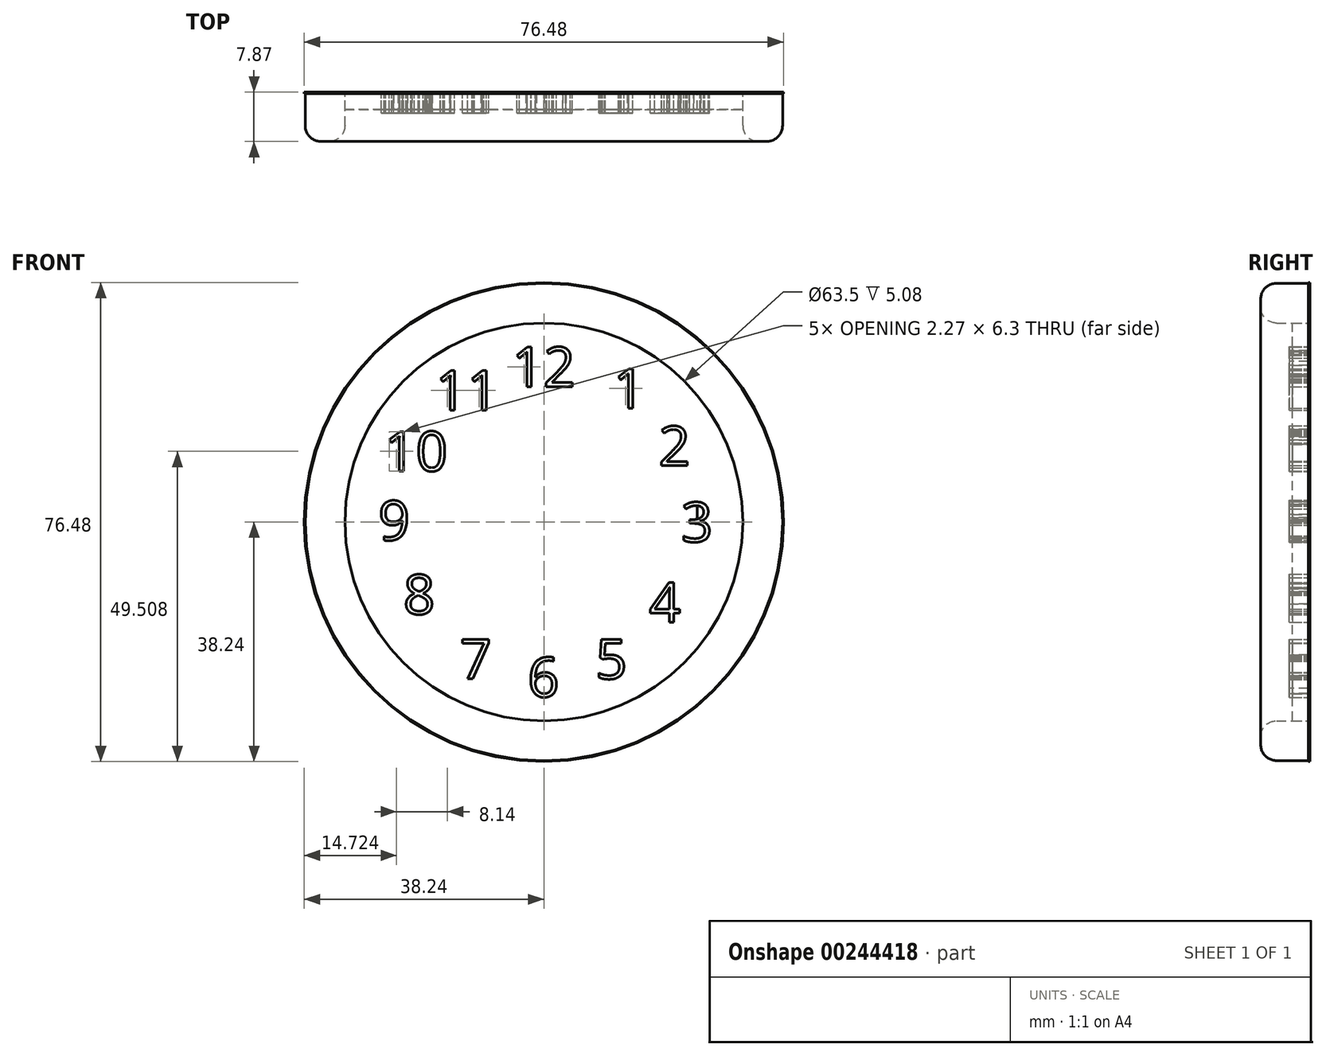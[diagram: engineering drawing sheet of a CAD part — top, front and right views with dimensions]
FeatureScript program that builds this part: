
annotation { "Feature Type Name" : "Feature", "Feature Type Description" : "" }
export const myFeature = defineFeature(function(context is Context, id is Id, definition is map)
    precondition{}
    {
        {
            var Q0;
            Q0=qCreatedBy(makeId("Front.planeOp"),FACE);
            var sketch = newSketch(context, id + "F0", { "sketchPlane" : qUnion([Q0])});
            skCircle(sketch, "E0", {"center": v(0, 0) * mm, "radius": 38.1 * mm});
            skCircle(sketch, "E1", {"center": v(0, 0) * mm, "radius": 31.75 * mm});
            skCircle(sketch, "E2", {"center": v(0, 0) * mm, "radius": 1.27 * mm, "construction": true});
            skText(sketch, "E3", { "text": "12", "fontName": "OpenSans-Regular.ttf"});
            skText(sketch, "E4", { "text": "1\n", "fontName": "OpenSans-Regular.ttf"});
            skText(sketch, "E5", { "text": "2", "fontName": "OpenSans-Regular.ttf"});
            skText(sketch, "E6", { "text": "10", "fontName": "OpenSans-Regular.ttf"});
            skText(sketch, "E7", { "text": "11", "fontName": "OpenSans-Regular.ttf"});
            skText(sketch, "E8", { "text": "4", "fontName": "OpenSans-Regular.ttf"});
            skText(sketch, "E9", { "text": "3", "fontName": "OpenSans-Regular.ttf"});
            skLineSegment(sketch, "E10", {"start": v(24.46, 0) * mm, "end": v(24.46, 3.18) * mm});
            skLineSegment(sketch, "E11", {"start": v(-23.86, 0) * mm, "end": v(-23.86, 3.42) * mm, "construction": true});
            skText(sketch, "E12", { "text": "5", "fontName": "OpenSans-Regular.ttf"});
            skText(sketch, "E13", { "text": "6", "fontName": "OpenSans-Regular.ttf"});
            skText(sketch, "E14", { "text": "9", "fontName": "OpenSans-Regular.ttf"});
            skText(sketch, "E15", { "text": "7", "fontName": "OpenSans-Regular.ttf"});
            skText(sketch, "E16", { "text": "8", "fontName": "OpenSans-Regular.ttf"});
            const initialGuessF0  = {"E3": [-0.0051, 0.0216, 1, 0, 0.00635], "E4": [0.0111, 0.01815, 1, 0, 0.00635], "E5": [0.01832, 0.00897, 1, 0, 0.00635], "E6": [-0.02546, 0.00812, 1, 0, 0.00635], "E7": [-0.01732, 0.01785, 1, 0, 0.00635], "E8": [0.0168, -0.016, 1, 0, 0.00635], "E9": [0.0219, -0.00318, 1, 0, 0.00635], "E12": [0.00824, -0.02505, 1, 0, 0.00635], "E13": [-0.0026, -0.02794, 1, 0, 0.00635], "E14": [-0.02643, -0.00293, 1, 0, 0.00635], "E15": [-0.01338, -0.02505, 1, 0, 0.00635], "E16": [-0.02243, -0.01473, 1, 0, 0.00635]};
            skSetInitialGuess(sketch, initialGuessF0);
            skSolve(sketch);
        }
        {
            var Q0;
            Q0=makeQuery(id+"F0.imprint","IMPRINT",FACE,{"disambiguationData":[TD([[makeQuery(id+"F0.imprint","IMPRINT",EDGE,{"derivedFrom":sQuery(id+"F0.wireOp",EDGE,"E0")}),1.0]])]});
            extrude(context, id + "F1", {"entities" : qUnion([Q0]), "depth" : 7.62 * mm});
        }
        {
            var Q0;
            Q0=makeQuery(id+"F0.imprint","IMPRINT",FACE,{"disambiguationData":[TD([[makeQuery(id+"F0.imprint","IMPRINT",EDGE,{"derivedFrom":sQuery(id+"F0.wireOp",EDGE,"E6.sketch_text.stroke-17")}),1.0]])]});
            extrude(context, id + "F2", {"entities" : qUnion([Q0]), "depth" : 2.54 * mm});
        }
        {
            var Q0;
            Q0=makeQuery(id+"F0.imprint","IMPRINT",FACE,{"disambiguationData":[TD([[makeQuery(id+"F0.imprint","IMPRINT",EDGE,{"derivedFrom":sQuery(id+"F0.wireOp",EDGE,"E8.sketch_text.stroke-11")}),1.0]])]});
            extrude(context, id + "F3", {"entities" : qUnion([Q0]), "depth" : 2.54 * mm});
        }
        {
            var Q0;
            Q0=makeQuery(id+"F0.imprint","IMPRINT",FACE,{"disambiguationData":[TD([[makeQuery(id+"F0.imprint","IMPRINT",EDGE,{"derivedFrom":sQuery(id+"F0.wireOp",EDGE,"E14.sketch_text.stroke-16")}),1.0]])]});
            extrude(context, id + "F4", {"entities" : qUnion([Q0]), "depth" : 2.54 * mm});
        }
        {
            var Q0;
            Q0=makeQuery(id+"F0.imprint","IMPRINT",FACE,{"disambiguationData":[TD([[makeQuery(id+"F0.imprint","IMPRINT",EDGE,{"derivedFrom":sQuery(id+"F0.wireOp",EDGE,"E13.sketch_text.stroke-15")}),1.0]])]});
            var Q1;
            Q1=makeQuery(id+"F0.imprint","IMPRINT",FACE,{"disambiguationData":[TD([[makeQuery(id+"F0.imprint","IMPRINT",EDGE,{"derivedFrom":sQuery(id+"F0.wireOp",EDGE,"E16.sketch_text.stroke-15")}),1.0]])]});
            var Q2;
            Q2=makeQuery(id+"F0.imprint","IMPRINT",FACE,{"disambiguationData":[TD([[makeQuery(id+"F0.imprint","IMPRINT",EDGE,{"derivedFrom":sQuery(id+"F0.wireOp",EDGE,"E16.sketch_text.stroke-23")}),1.0]])]});
            extrude(context, id + "F5", {"entities" : qUnion([Q0, Q1, Q2]), "depth" : 2.54 * mm});
        }
        {
            var Q0;
            Q0=makeQuery(id+"F0.imprint","IMPRINT",FACE,{"disambiguationData":[TD([[makeQuery(id+"F0.imprint","IMPRINT",EDGE,{"derivedFrom":sQuery(id+"F0.wireOp",EDGE,"E9.sketch_text.stroke-0")}),-1.0]])]});
            var Q1;
            Q1=makeQuery(id+"F0.imprint","IMPRINT",FACE,{"disambiguationData":[TD([[makeQuery(id+"F0.imprint","IMPRINT",EDGE,{"derivedFrom":sQuery(id+"F0.wireOp",EDGE,"E8.sketch_text.stroke-0")}),-1.0]])]});
            var Q2;
            Q2=makeQuery(id+"F0.imprint","IMPRINT",FACE,{"disambiguationData":[TD([[makeQuery(id+"F0.imprint","IMPRINT",EDGE,{"derivedFrom":sQuery(id+"F0.wireOp",EDGE,"E12.sketch_text.stroke-0")}),-1.0]])]});
            var Q3;
            Q3=makeQuery(id+"F0.imprint","IMPRINT",FACE,{"disambiguationData":[TD([[makeQuery(id+"F0.imprint","IMPRINT",EDGE,{"derivedFrom":sQuery(id+"F0.wireOp",EDGE,"E13.sketch_text.stroke-0")}),-1.0]])]});
            var Q4;
            Q4=makeQuery(id+"F0.imprint","IMPRINT",FACE,{"disambiguationData":[TD([[makeQuery(id+"F0.imprint","IMPRINT",EDGE,{"derivedFrom":sQuery(id+"F0.wireOp",EDGE,"E15.sketch_text.stroke-0")}),-1.0]])]});
            var Q5;
            Q5=makeQuery(id+"F0.imprint","IMPRINT",FACE,{"disambiguationData":[TD([[makeQuery(id+"F0.imprint","IMPRINT",EDGE,{"derivedFrom":sQuery(id+"F0.wireOp",EDGE,"E16.sketch_text.stroke-0")}),-1.0]])]});
            var Q6;
            Q6=makeQuery(id+"F0.imprint","IMPRINT",FACE,{"disambiguationData":[TD([[makeQuery(id+"F0.imprint","IMPRINT",EDGE,{"derivedFrom":sQuery(id+"F0.wireOp",EDGE,"E14.sketch_text.stroke-0")}),-1.0]])]});
            var Q7;
            Q7=makeQuery(id+"F0.imprint","IMPRINT",FACE,{"disambiguationData":[TD([[makeQuery(id+"F0.imprint","IMPRINT",EDGE,{"derivedFrom":sQuery(id+"F0.wireOp",EDGE,"E6.sketch_text.stroke-9")}),-1.0]])]});
            var Q8;
            Q8=makeQuery(id+"F0.imprint","IMPRINT",FACE,{"disambiguationData":[TD([[makeQuery(id+"F0.imprint","IMPRINT",EDGE,{"derivedFrom":sQuery(id+"F0.wireOp",EDGE,"E6.sketch_text.stroke-0")}),-1.0]])]});
            var Q9;
            Q9=makeQuery(id+"F0.imprint","IMPRINT",FACE,{"disambiguationData":[TD([[makeQuery(id+"F0.imprint","IMPRINT",EDGE,{"derivedFrom":sQuery(id+"F0.wireOp",EDGE,"E5.sketch_text.stroke-0")}),-1.0]])]});
            var Q10;
            Q10=makeQuery(id+"F0.imprint","IMPRINT",FACE,{"disambiguationData":[TD([[makeQuery(id+"F0.imprint","IMPRINT",EDGE,{"derivedFrom":sQuery(id+"F0.wireOp",EDGE,"E4.sketch_text.stroke-0")}),-1.0]])]});
            var Q11;
            Q11=makeQuery(id+"F0.imprint","IMPRINT",FACE,{"disambiguationData":[TD([[makeQuery(id+"F0.imprint","IMPRINT",EDGE,{"derivedFrom":sQuery(id+"F0.wireOp",EDGE,"E3.sketch_text.stroke-9")}),-1.0]])]});
            var Q12;
            Q12=makeQuery(id+"F0.imprint","IMPRINT",FACE,{"disambiguationData":[TD([[makeQuery(id+"F0.imprint","IMPRINT",EDGE,{"derivedFrom":sQuery(id+"F0.wireOp",EDGE,"E3.sketch_text.stroke-0")}),-1.0]])]});
            var Q13;
            Q13=makeQuery(id+"F0.imprint","IMPRINT",FACE,{"disambiguationData":[TD([[makeQuery(id+"F0.imprint","IMPRINT",EDGE,{"derivedFrom":sQuery(id+"F0.wireOp",EDGE,"E7.sketch_text.stroke-9")}),-1.0]])]});
            var Q14;
            Q14=makeQuery(id+"F0.imprint","IMPRINT",FACE,{"disambiguationData":[TD([[makeQuery(id+"F0.imprint","IMPRINT",EDGE,{"derivedFrom":sQuery(id+"F0.wireOp",EDGE,"E7.sketch_text.stroke-0")}),-1.0]])]});
            extrude(context, id + "F6", {"entities" : qUnion([Q0, Q1, Q2, Q3, Q4, Q5, Q6, Q7, Q8, Q9, Q10, Q11, Q12, Q13, Q14]), "depth" : 3.07 * mm});
        }
        {
            var Q0;
            Q0=makeQuery(id+"F1.opExtrude","CAP_EDGE",EDGE,{"disambiguationData":[OSD([sQuery(id+"F0.wireOp",EDGE,"E0")])],"isStart":false});
            var Q1;
            Q1=makeQuery(id+"F1.opExtrude","CAP_FACE",FACE,{"disambiguationData":[OSD([sQuery(id+"F0.wireOp",EDGE,"E0"),sQuery(id+"F0.wireOp",EDGE,"E1")])],"isStart":false});
            fillet(context, id + "F7", {"entities" : qUnion([Q0, Q1]), "radius" : 2.54 * mm, "tangentPropagation" : true, "allowEdgeOverflow" : false});
        }
        {
            var Q0;
            Q0=makeQuery(id+"F0.imprint","IMPRINT",FACE,{"disambiguationData":[TD([[makeQuery(id+"F0.imprint","IMPRINT",EDGE,{"derivedFrom":sQuery(id+"F0.wireOp",EDGE,"E1")}),1.0]])]});
            extrude(context, id + "F8", {"entities" : qUnion([Q0]), "depth" : 2.54 * mm});
        }
        {
            var Q0;
            {var subQ4=sQuery(id+"F0.wireOp",EDGE,"E9.sketch_text.stroke-18");Q0=makeQuery(id+"F0.imprint","IMPRINT",FACE,{"disambiguationData":[TD([[makeQuery(id+"F0.imprint","IMPRINT",EDGE,{"derivedFrom":subQ4}),1.0]])]});}
            extrude(context, id + "F9", {"entities" : qUnion([Q0]), "depth" : 2.54 * mm});
        }
        {
            var Q0;
            Q0=qCreatedBy(makeId("Front.planeOp"),FACE);
            var sketch = newSketch(context, id + "F10", { "sketchPlane" : qUnion([Q0])});
            skCircle(sketch, "E17", {"center": v(0, 0) * mm, "radius": 38.24 * mm});
            skSolve(sketch);
        }
        {
            var Q0;
            Q0 = qSketchRegion(id + "F10", true);
            extrude(context, id + "F11", {"entities" : qUnion([Q0]), "oppositeDirection" : true, "depth" : 0.25 * mm});
        }
    });
